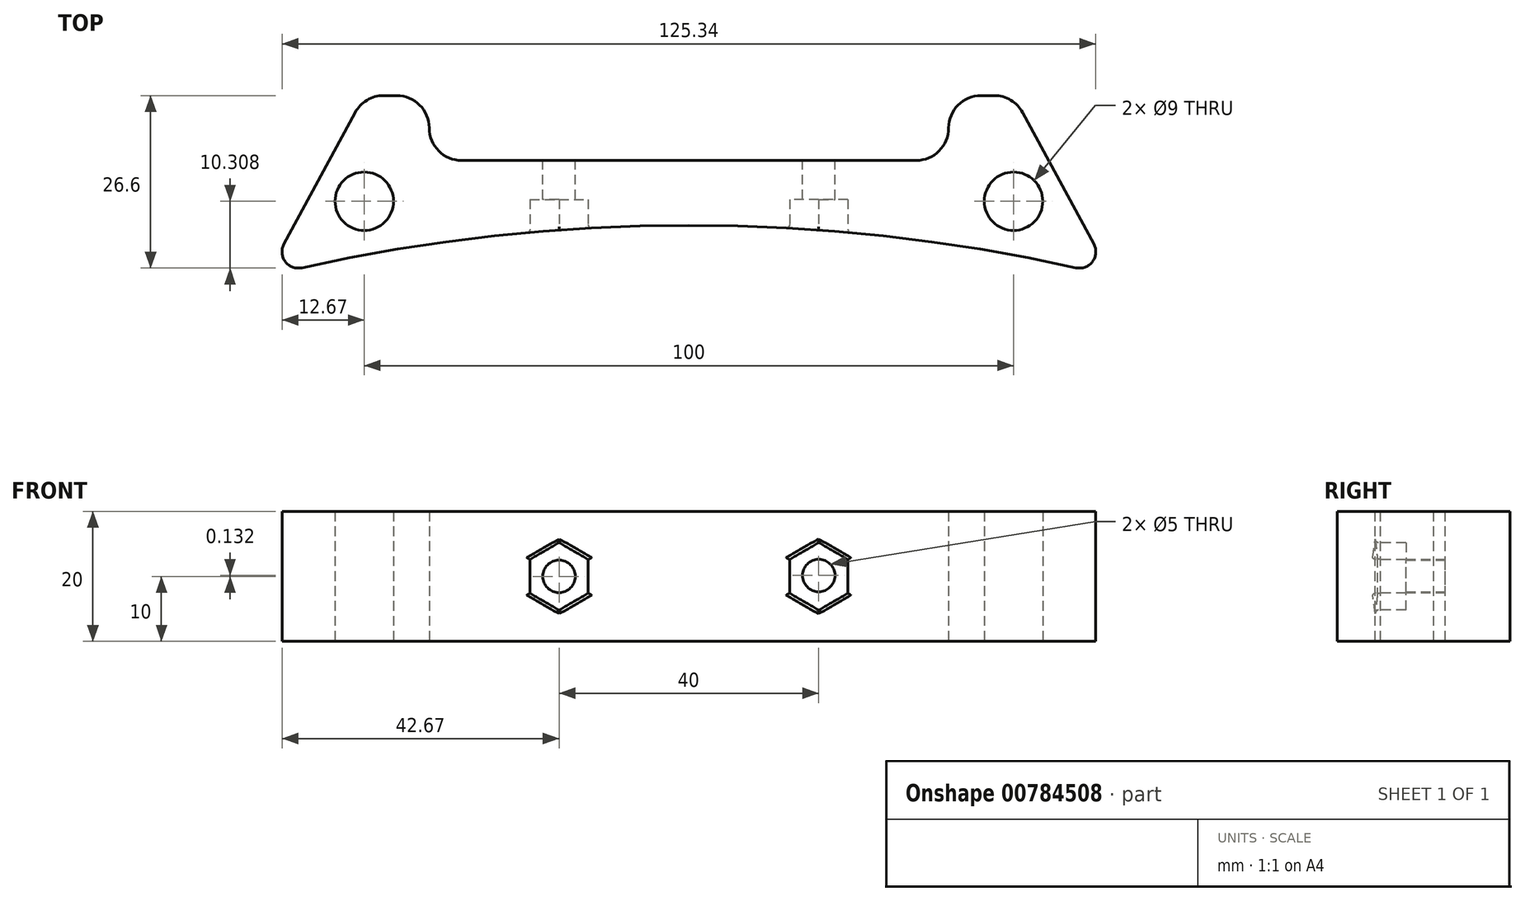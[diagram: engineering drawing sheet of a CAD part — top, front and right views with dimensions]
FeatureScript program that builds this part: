
annotation { "Feature Type Name" : "Feature", "Feature Type Description" : "" }
export const myFeature = defineFeature(function(context is Context, id is Id, definition is map)
    precondition{}
    {
        {
            var Q0;
            Q0=qCreatedBy(makeId("Top.planeOp"),FACE);
            var sketch = newSketch(context, id + "F0", { "sketchPlane" : qUnion([Q0])});
            skPoint(sketch, "E0.middle", {"position": v(0, 0) * mm});
            skLineSegment(sketch, "E1.top", {"start": v(-40, 0) * mm, "end": v(40, 0) * mm});
            skLineSegment(sketch, "E1.left", {"start": v(-40, 10) * mm, "end": v(-40, 0) * mm});
            skLineSegment(sketch, "E1.right", {"start": v(40, 10) * mm, "end": v(40, 0) * mm});
            skLineSegment(sketch, "E2", {"start": v(-40, 10) * mm, "end": v(-50, 10) * mm});
            skLineSegment(sketch, "E3", {"start": v(40, 10) * mm, "end": v(50, 10) * mm});
            skLineSegment(sketch, "E4", {"start": v(0, 0) * mm, "end": v(0, -10) * mm, "construction": true});
            skArc(sketch, "E5", {"start": v(65, -17.8) * mm, "mid": v(0, -10) * mm, "end": v(-65, -17.8) * mm});
            skLineSegment(sketch, "E6", {"start": v(-65, -17.8) * mm, "end": v(-50, 10) * mm});
            skLineSegment(sketch, "E7", {"start": v(50, 10) * mm, "end": v(65, -17.8) * mm});
            skCircle(sketch, "E8", {"center": v(-50, -6.3) * mm, "radius": 4.5 * mm});
            skCircle(sketch, "E9", {"center": v(50, -6.3) * mm, "radius": 4.5 * mm});
            skSolve(sketch);
        }
        {
            var Q0;
            Q0=makeQuery(id+"F0.imprint","IMPRINT",FACE,{"disambiguationData":[TD([[makeQuery(id+"F0.imprint","IMPRINT",EDGE,{"derivedFrom":sQuery(id+"F0.wireOp",EDGE,"E0.bottom")}),1.0]])]});
            var Q1;
            Q1=makeQuery(id+"F0.imprint","IMPRINT",FACE,{"disambiguationData":[TD([[makeQuery(id+"F0.imprint","IMPRINT",EDGE,{"derivedFrom":sQuery(id+"F0.wireOp",EDGE,"E1.top")}),-1.0]])]});
            extrude(context, id + "F1", {"entities" : qUnion([Q0, Q1]), "depth" : 20 * mm, "offsetDistance" : 25 * mm});
        }
        {
            var Q0;
            Q0=makeQuery(id+"F1.opExtrude","SWEPT_EDGE",EDGE,{"disambiguationData":[OSD([sQuery(id+"F0.wireOp",EDGE,"E2"),sQuery(id+"F0.wireOp",EDGE,"MfdlSLqY-4P84-FQ1d-JYDe-RKYDkFxBH7FF")])]});
            var Q1;
            Q1=makeQuery(id+"F1.opExtrude","SWEPT_EDGE",EDGE,{"disambiguationData":[OSD([sQuery(id+"F0.wireOp",EDGE,"E1.left"),sQuery(id+"F0.wireOp",EDGE,"E2")])]});
            var Q2;
            Q2=makeQuery(id+"F1.opExtrude","SWEPT_EDGE",EDGE,{"disambiguationData":[OSD([sQuery(id+"F0.wireOp",EDGE,"E1.top"),sQuery(id+"F0.wireOp",EDGE,"E1.left")])]});
            var Q3;
            Q3=makeQuery(id+"F1.opExtrude","SWEPT_EDGE",EDGE,{"disambiguationData":[OSD([sQuery(id+"F0.wireOp",EDGE,"E1.right"),sQuery(id+"F0.wireOp",EDGE,"E3")])]});
            var Q4;
            Q4=makeQuery(id+"F1.opExtrude","SWEPT_EDGE",EDGE,{"disambiguationData":[OSD([sQuery(id+"F0.wireOp",EDGE,"E3"),sQuery(id+"F0.wireOp",EDGE,"3Oll6O0g-8p98-aHoA-joHb-zCk68E6HXgNw")])]});
            var Q5;
            Q5=makeQuery(id+"F1.opExtrude","SWEPT_EDGE",EDGE,{"disambiguationData":[OSD([sQuery(id+"F0.wireOp",EDGE,"E1.top"),sQuery(id+"F0.wireOp",EDGE,"E1.right")])]});
            fillet(context, id + "F2", {"entities" : qUnion([Q0, Q1, Q2, Q3, Q4, Q5]), "radius" : 5 * mm, "tangentPropagation" : true, "allowEdgeOverflow" : false});
        }
        {
            var Q0;
            Q0=makeQuery(id+"F1.opExtrude","SWEPT_EDGE",EDGE,{"disambiguationData":[OSD([sQuery(id+"F0.wireOp",EDGE,"E5"),sQuery(id+"F0.wireOp",EDGE,"E6")])]});
            var Q1;
            Q1=makeQuery(id+"F1.opExtrude","SWEPT_EDGE",EDGE,{"disambiguationData":[OSD([sQuery(id+"F0.wireOp",EDGE,"E5"),sQuery(id+"F0.wireOp",EDGE,"E7")])]});
            fillet(context, id + "F3", {"entities" : qUnion([Q0, Q1]), "radius" : 2.5 * mm, "tangentPropagation" : true, "allowEdgeOverflow" : false});
        }
        {
            var Q0;
            Q0=makeQuery(id+"F1.opExtrude","SWEPT_FACE",FACE,{"disambiguationData":[OSD([sQuery(id+"F0.wireOp",EDGE,"E1.top")])]});
            var sketch = newSketch(context, id + "F4", { "sketchPlane" : qUnion([Q0])});
            skCircle(sketch, "E10", {"center": v(0, 10) * mm, "radius": 20 * mm, "construction": true});
            skCircle(sketch, "E11", {"center": v(-20, 10.13) * mm, "radius": 2.5 * mm});
            skCircle(sketch, "E12", {"center": v(20, 10) * mm, "radius": 2.5 * mm});
            skSolve(sketch);
        }
        {
            var Q0;
            Q0=makeQuery(id+"F4.imprint","IMPRINT",FACE,{"disambiguationData":[TD([[makeQuery(id+"F4.imprint","IMPRINT",EDGE,{"derivedFrom":sQuery(id+"F4.wireOp",EDGE,"E11")}),1.0]])]});
            var Q1;
            Q1=makeQuery(id+"F4.imprint","IMPRINT",FACE,{"disambiguationData":[TD([[makeQuery(id+"F4.imprint","IMPRINT",EDGE,{"derivedFrom":sQuery(id+"F4.wireOp",EDGE,"E12")}),1.0]])]});
            var Q2;
            Q2=sQuery(id+"F4.wireOp",EDGE,"E12");
            var Q3;
            Q3=sQuery(id+"F4.wireOp",EDGE,"E11");
            extrude(context, id + "F5", {"entities" : qUnion([Q0, Q1]), "operationType" : NewBodyOperationType.REMOVE, "surfaceEntities" : qUnion([Q2, Q3]), "oppositeDirection" : true, "depth" : 25 * mm, "offsetDistance" : 25 * mm});
        }
        {
            var Q0;
            Q0=qCreatedBy(makeId("Front.planeOp"),FACE);
            cPlane(context, id + "F6", {"entities" : qUnion([Q0]), "cplaneType" : CPlaneType.OFFSET, "offset" : 12 * mm, "width" : 150 * mm, "height" : 150 * mm});
        }
        {
            var Q0;
            Q0=qCreatedBy(id+"F6.planeOp",FACE);
            var sketch = newSketch(context, id + "F7", { "sketchPlane" : qUnion([Q0])});
            skCircle(sketch, "E13", {"center": v(0, 10) * mm, "radius": 20 * mm, "construction": true});
            skCircle(sketch, "E14.cCircle", {"center": v(-20, 10) * mm, "radius": 4.5 * mm, "construction": true});
            skLineSegment(sketch, "E14.0", {"start": v(-15.5, 12.6) * mm, "end": v(-15.5, 7.4) * mm});
            skLineSegment(sketch, "E14.1", {"start": v(-15.5, 7.4) * mm, "end": v(-20, 4.8) * mm});
            skLineSegment(sketch, "E14.2", {"start": v(-20, 4.8) * mm, "end": v(-24.5, 7.4) * mm});
            skLineSegment(sketch, "E14.3", {"start": v(-24.5, 7.4) * mm, "end": v(-24.5, 12.6) * mm});
            skLineSegment(sketch, "E14.4", {"start": v(-24.5, 12.6) * mm, "end": v(-20, 15.2) * mm});
            skLineSegment(sketch, "E14.5", {"start": v(-20, 15.2) * mm, "end": v(-15.5, 12.6) * mm});
            skPoint(sketch, "E14.0.midPoint", {"position": v(-15.5, 10) * mm});
            skCircle(sketch, "E15.cCircle", {"center": v(20, 10) * mm, "radius": 4.5 * mm, "construction": true});
            skLineSegment(sketch, "E15.0", {"start": v(15.5, 7.4) * mm, "end": v(15.5, 12.6) * mm});
            skLineSegment(sketch, "E15.1", {"start": v(15.5, 12.6) * mm, "end": v(20, 15.2) * mm});
            skLineSegment(sketch, "E15.2", {"start": v(20, 15.2) * mm, "end": v(24.5, 12.6) * mm});
            skLineSegment(sketch, "E15.3", {"start": v(24.5, 12.6) * mm, "end": v(24.5, 7.4) * mm});
            skLineSegment(sketch, "E15.4", {"start": v(24.5, 7.4) * mm, "end": v(20, 4.8) * mm});
            skLineSegment(sketch, "E15.5", {"start": v(20, 4.8) * mm, "end": v(15.5, 7.4) * mm});
            skPoint(sketch, "E15.0.midPoint", {"position": v(15.5, 10) * mm});
            skSolve(sketch);
        }
        {
            var Q0;
            Q0=makeQuery(id+"F7.imprint","IMPRINT",FACE,{"disambiguationData":[TD([[makeQuery(id+"F7.imprint","IMPRINT",EDGE,{"derivedFrom":sQuery(id+"F7.wireOp",EDGE,"E14.0")}),-1.0]])]});
            var Q1;
            Q1=makeQuery(id+"F7.imprint","IMPRINT",FACE,{"disambiguationData":[TD([[makeQuery(id+"F7.imprint","IMPRINT",EDGE,{"derivedFrom":sQuery(id+"F7.wireOp",EDGE,"E15.0")}),-1.0]])]});
            extrude(context, id + "F8", {"entities" : qUnion([Q0, Q1]), "operationType" : NewBodyOperationType.REMOVE, "oppositeDirection" : true, "depth" : 6 * mm, "offsetDistance" : 25 * mm});
        }
        {
            var Q0;
            Q0=makeQuery(id+"F8.boolean.opBoolean","INTERSECT",EDGE,{"derivedFrom":[makeQuery(id+"F1.opExtrude","SWEPT_FACE",FACE,{"disambiguationData":[OSD([sQuery(id+"F0.wireOp",EDGE,"E5")])]}),makeQuery(id+"F8.opExtrude","SWEPT_FACE",FACE,{"disambiguationData":[OSD([sQuery(id+"F7.wireOp",EDGE,"E14.4")])]})]});
            var Q1;
            Q1=makeQuery(id+"F8.boolean.opBoolean","INTERSECT",EDGE,{"derivedFrom":[makeQuery(id+"F1.opExtrude","SWEPT_FACE",FACE,{"disambiguationData":[OSD([sQuery(id+"F0.wireOp",EDGE,"E5")])]}),makeQuery(id+"F8.opExtrude","SWEPT_FACE",FACE,{"disambiguationData":[OSD([sQuery(id+"F7.wireOp",EDGE,"E14.3")])]})]});
            var Q2;
            Q2=makeQuery(id+"F8.boolean.opBoolean","INTERSECT",EDGE,{"derivedFrom":[makeQuery(id+"F1.opExtrude","SWEPT_FACE",FACE,{"disambiguationData":[OSD([sQuery(id+"F0.wireOp",EDGE,"E5")])]}),makeQuery(id+"F8.opExtrude","SWEPT_FACE",FACE,{"disambiguationData":[OSD([sQuery(id+"F7.wireOp",EDGE,"E14.2")])]})]});
            var Q3;
            Q3=makeQuery(id+"F8.boolean.opBoolean","INTERSECT",EDGE,{"derivedFrom":[makeQuery(id+"F1.opExtrude","SWEPT_FACE",FACE,{"disambiguationData":[OSD([sQuery(id+"F0.wireOp",EDGE,"E5")])]}),makeQuery(id+"F8.opExtrude","SWEPT_FACE",FACE,{"disambiguationData":[OSD([sQuery(id+"F7.wireOp",EDGE,"E14.1")])]})]});
            var Q4;
            Q4=makeQuery(id+"F8.boolean.opBoolean","INTERSECT",EDGE,{"derivedFrom":[makeQuery(id+"F1.opExtrude","SWEPT_FACE",FACE,{"disambiguationData":[OSD([sQuery(id+"F0.wireOp",EDGE,"E5")])]}),makeQuery(id+"F8.opExtrude","SWEPT_FACE",FACE,{"disambiguationData":[OSD([sQuery(id+"F7.wireOp",EDGE,"E14.0")])]})]});
            var Q5;
            Q5=makeQuery(id+"F8.boolean.opBoolean","INTERSECT",EDGE,{"derivedFrom":[makeQuery(id+"F1.opExtrude","SWEPT_FACE",FACE,{"disambiguationData":[OSD([sQuery(id+"F0.wireOp",EDGE,"E5")])]}),makeQuery(id+"F8.opExtrude","SWEPT_FACE",FACE,{"disambiguationData":[OSD([sQuery(id+"F7.wireOp",EDGE,"E14.5")])]})]});
            var Q6;
            Q6=makeQuery(id+"F8.boolean.opBoolean","INTERSECT",EDGE,{"derivedFrom":[makeQuery(id+"F1.opExtrude","SWEPT_FACE",FACE,{"disambiguationData":[OSD([sQuery(id+"F0.wireOp",EDGE,"E5")])]}),makeQuery(id+"F8.opExtrude","SWEPT_FACE",FACE,{"disambiguationData":[OSD([sQuery(id+"F7.wireOp",EDGE,"E15.1")])]})]});
            var Q7;
            Q7=makeQuery(id+"F8.boolean.opBoolean","INTERSECT",EDGE,{"derivedFrom":[makeQuery(id+"F1.opExtrude","SWEPT_FACE",FACE,{"disambiguationData":[OSD([sQuery(id+"F0.wireOp",EDGE,"E5")])]}),makeQuery(id+"F8.opExtrude","SWEPT_FACE",FACE,{"disambiguationData":[OSD([sQuery(id+"F7.wireOp",EDGE,"E15.0")])]})]});
            var Q8;
            Q8=makeQuery(id+"F8.boolean.opBoolean","INTERSECT",EDGE,{"derivedFrom":[makeQuery(id+"F1.opExtrude","SWEPT_FACE",FACE,{"disambiguationData":[OSD([sQuery(id+"F0.wireOp",EDGE,"E5")])]}),makeQuery(id+"F8.opExtrude","SWEPT_FACE",FACE,{"disambiguationData":[OSD([sQuery(id+"F7.wireOp",EDGE,"E15.5")])]})]});
            var Q9;
            Q9=makeQuery(id+"F8.boolean.opBoolean","INTERSECT",EDGE,{"derivedFrom":[makeQuery(id+"F1.opExtrude","SWEPT_FACE",FACE,{"disambiguationData":[OSD([sQuery(id+"F0.wireOp",EDGE,"E5")])]}),makeQuery(id+"F8.opExtrude","SWEPT_FACE",FACE,{"disambiguationData":[OSD([sQuery(id+"F7.wireOp",EDGE,"E15.4")])]})]});
            var Q10;
            Q10=makeQuery(id+"F8.boolean.opBoolean","INTERSECT",EDGE,{"derivedFrom":[makeQuery(id+"F1.opExtrude","SWEPT_FACE",FACE,{"disambiguationData":[OSD([sQuery(id+"F0.wireOp",EDGE,"E5")])]}),makeQuery(id+"F8.opExtrude","SWEPT_FACE",FACE,{"disambiguationData":[OSD([sQuery(id+"F7.wireOp",EDGE,"E15.3")])]})]});
            var Q11;
            Q11=makeQuery(id+"F8.boolean.opBoolean","INTERSECT",EDGE,{"derivedFrom":[makeQuery(id+"F1.opExtrude","SWEPT_FACE",FACE,{"disambiguationData":[OSD([sQuery(id+"F0.wireOp",EDGE,"E5")])]}),makeQuery(id+"F8.opExtrude","SWEPT_FACE",FACE,{"disambiguationData":[OSD([sQuery(id+"F7.wireOp",EDGE,"E15.2")])]})]});
            fillet(context, id + "F9", {"entities" : qUnion([Q0, Q1, Q2, Q3, Q4, Q5, Q6, Q7, Q8, Q9, Q10, Q11]), "radius" : 0.5 * mm, "tangentPropagation" : true, "allowEdgeOverflow" : false});
        }
    });
